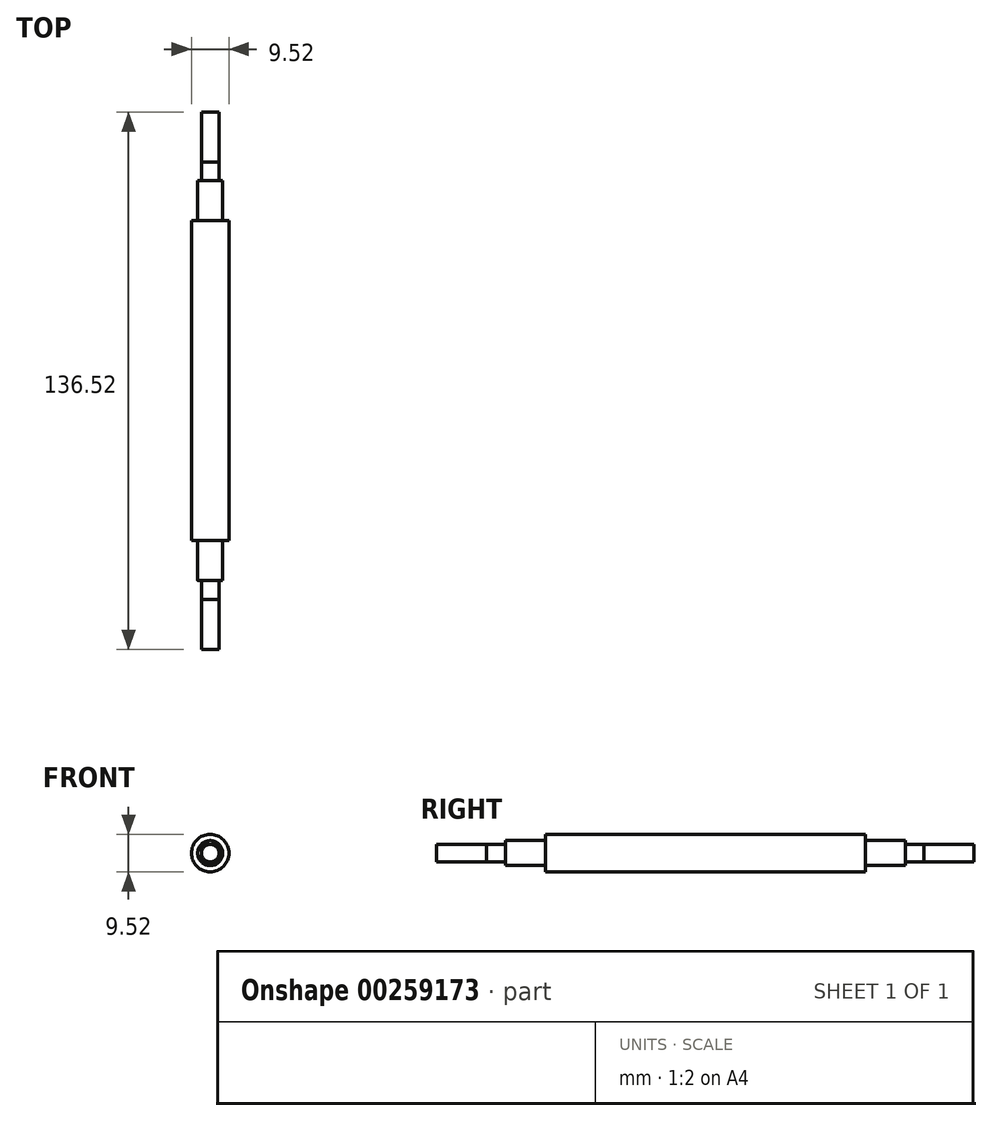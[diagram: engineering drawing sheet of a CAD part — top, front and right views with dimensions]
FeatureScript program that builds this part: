
annotation { "Feature Type Name" : "Feature", "Feature Type Description" : "" }
export const myFeature = defineFeature(function(context is Context, id is Id, definition is map)
    precondition{}
    {
        {
            var Q0;
            Q0=qCreatedBy(makeId("Front.planeOp"),FACE);
            var sketch = newSketch(context, id + "F0", { "sketchPlane" : qUnion([Q0])});
            skCircle(sketch, "E0", {"center": v(0, 0) * mm, "radius": 3.18 * mm});
            skSolve(sketch);
        }
        {
            var Q0;
            Q0 = qSketchRegion(id + "F0", true);
            extrude(context, id + "F1", {"entities" : qUnion([Q0]), "depth" : 50.8 * mm});
        }
        {
            var Q0;
            Q0=makeQuery(id+"F1.opExtrude","CAP_FACE",FACE,{"disambiguationData":[OSD([sQuery(id+"F0.wireOp",EDGE,"E0")])],"isStart":false});
            var sketch = newSketch(context, id + "F2", { "sketchPlane" : qUnion([Q0])});
            skLineSegment(sketch, "E1.bottom", {"start": v(-2.25, 2.25) * mm, "end": v(2.25, 2.25) * mm});
            skLineSegment(sketch, "E1.top", {"start": v(-2.25, -2.25) * mm, "end": v(2.25, -2.25) * mm});
            skLineSegment(sketch, "E1.left", {"start": v(-2.25, 2.25) * mm, "end": v(-2.25, -2.25) * mm});
            skLineSegment(sketch, "E1.right", {"start": v(2.25, 2.25) * mm, "end": v(2.25, -2.25) * mm});
            skSolve(sketch);
        }
        {
            var Q0;
            Q0 = qSketchRegion(id + "F2", true);
            extrude(context, id + "F3", {"entities" : qUnion([Q0]), "operationType" : NewBodyOperationType.ADD, "depth" : 4.76 * mm});
        }
        {
            var Q0;
            Q0=makeQuery(id+"F3.opExtrude","CAP_FACE",FACE,{"disambiguationData":[OSD([sQuery(id+"F2.wireOp",EDGE,"E1.bottom"),sQuery(id+"F2.wireOp",EDGE,"E1.top"),sQuery(id+"F2.wireOp",EDGE,"E1.left"),sQuery(id+"F2.wireOp",EDGE,"E1.right")])],"isStart":false});
            var sketch = newSketch(context, id + "F4", { "sketchPlane" : qUnion([Q0])});
            skCircle(sketch, "E2", {"center": v(0, 0) * mm, "radius": 2.25 * mm});
            skLineSegment(sketch, "E3", {"start": v(-2.25, 2.25) * mm, "end": v(0, 0) * mm, "construction": true});
            skPoint(sketch, "E4", {"position": v(-1.59, 1.59) * mm});
            skSolve(sketch);
        }
        {
            var Q0;
            Q0 = qSketchRegion(id + "F4", true);
            extrude(context, id + "F5", {"entities" : qUnion([Q0]), "operationType" : NewBodyOperationType.ADD, "depth" : 12.7 * mm});
        }
        {
            var Q0;
            Q0=makeQuery(id+"F1.opExtrude","CAP_FACE",FACE,{"disambiguationData":[OSD([sQuery(id+"F0.wireOp",EDGE,"E0")])],"isStart":true});
            var sketch = newSketch(context, id + "F6", { "sketchPlane" : qUnion([Q0])});
            skCircle(sketch, "E5", {"center": v(0, 0) * mm, "radius": 4.76 * mm});
            skSolve(sketch);
        }
        {
            var Q0;
            Q0 = qSketchRegion(id + "F6", true);
            extrude(context, id + "F7", {"entities" : qUnion([Q0]), "operationType" : NewBodyOperationType.ADD, "oppositeDirection" : true, "depth" : 40.64 * mm});
        }
        {
            var Q0;
            Q0=makeQuery(id+"F1.opExtrude","SWEPT_BODY",BODY,{"disambiguationData":[OSD([sQuery(id+"F0.wireOp",EDGE,"E0")])]});
            var Q1;
            Q1=qCreatedBy(makeId("Front.planeOp"),FACE);
            mirror(context, id + "F8", {"operationType" : NewBodyOperationType.ADD, "entities" : qUnion([Q0]), "mirrorPlane" : qUnion([Q1])});
        }
    });
